FCSTD DOCUMENT  (FreeCAD 1.0R39109 (Git))
Label: Oblique Palette Case 
License: All rights reserved
LicenseURL: http://en.wikipedia.org/wiki/All_rights_reserved
objects: Sketcher::SketchObject×2, PartDesign::Body×1
note: 5 computed .brp shape members not serialized (recipe doc carries the construction recipe); baked Part::Feature solids carry a one-line shape summary decoded from their .brp

FEATURE [Sketcher::SketchObject] Sketch
  ArcFitTolerance = 1e-06
  AttachmentSupport = -> [YZ_Plane]
  FullyConstrained = false
  MakeInternals = false
  MapMode = 5
  Placement = pos=(0,0,0) rot=(0.57735,0.57735,0.57735;2.0944rad)
  sketch-geometry (8):
    g0: LineSegment StartX=-2.45182 StartY=-0.000505765 StartZ=0 EndX=0.000545166 EndY=-0.000505765 EndZ=0
    g1: LineSegment StartX=-1.99945 StartY=24.9995 StartZ=0 EndX=-1.99945 EndY=23.5995 EndZ=0
    g2: LineSegment StartX=0.000545166 StartY=-0.000505765 StartZ=0 EndX=0.000545166 EndY=23.5995 EndZ=0
    g3: LineSegment StartX=0.000545166 StartY=23.5995 StartZ=0 EndX=-1.99945 EndY=23.5995 EndZ=0
    g4: LineSegment StartX=-1.99945 StartY=24.9995 StartZ=0 EndX=-2.99945 EndY=24.9995 EndZ=0
    g5: LineSegment StartX=-2.99945 StartY=24.9995 StartZ=0 EndX=-4.99945 EndY=22.9995 EndZ=0
    g6: LineSegment StartX=-4.99945 StartY=22.9995 StartZ=0 EndX=-4.99945 EndY=2.54713 EndZ=0
    g7: LineSegment StartX=-4.99945 StartY=2.54713 StartZ=0 EndX=-2.45182 EndY=-0.000505765 EndZ=0
  constraints (21):
    c: Angle(g0,g7) = 2.35619
    c: Angle(g6,g5) = 2.35619
    c: Coincident(g5,g6)
    c: Coincident(g6,g7)
    c: Coincident(g7,g0)
    c: Coincident(g0,g2)
    c: DistanceX(g6,g0) = 5
    c: Coincident(g4,g5)
    c: Coincident(g2,g3)
    c: Coincident(g3,g1)
    c: DistanceX(g3,g3) = 2
    c: Coincident(g4,g1)
    c: DistanceY(g1,g1) = 1.4
    c: Angle(g5,g4) = 2.35619
    c: Perpendicular(g1,g4)
    c: Perpendicular(g3,g1)
    c: Perpendicular(g0,g2)
    c: DistanceX(g4,g4) = 1
    c: Vertical(g2)
    c: Horizontal(g3)
    c: DistanceY(g0,g1) = 25
FEATURE [Sketcher::SketchObject] Sketch001
  ArcFitTolerance = 1e-06
  AttachmentSupport = -> [XZ_Plane]
  FullyConstrained = true
  MakeInternals = false
  MapMode = 5
  Placement = pos=(0,0,0) rot=(1,0,0;1.5708rad)
FEATURE [PartDesign::Body] Body
  AllowCompound = false
  Group = -> [Sketch,Sketch001]
  Origin = -> Origin
